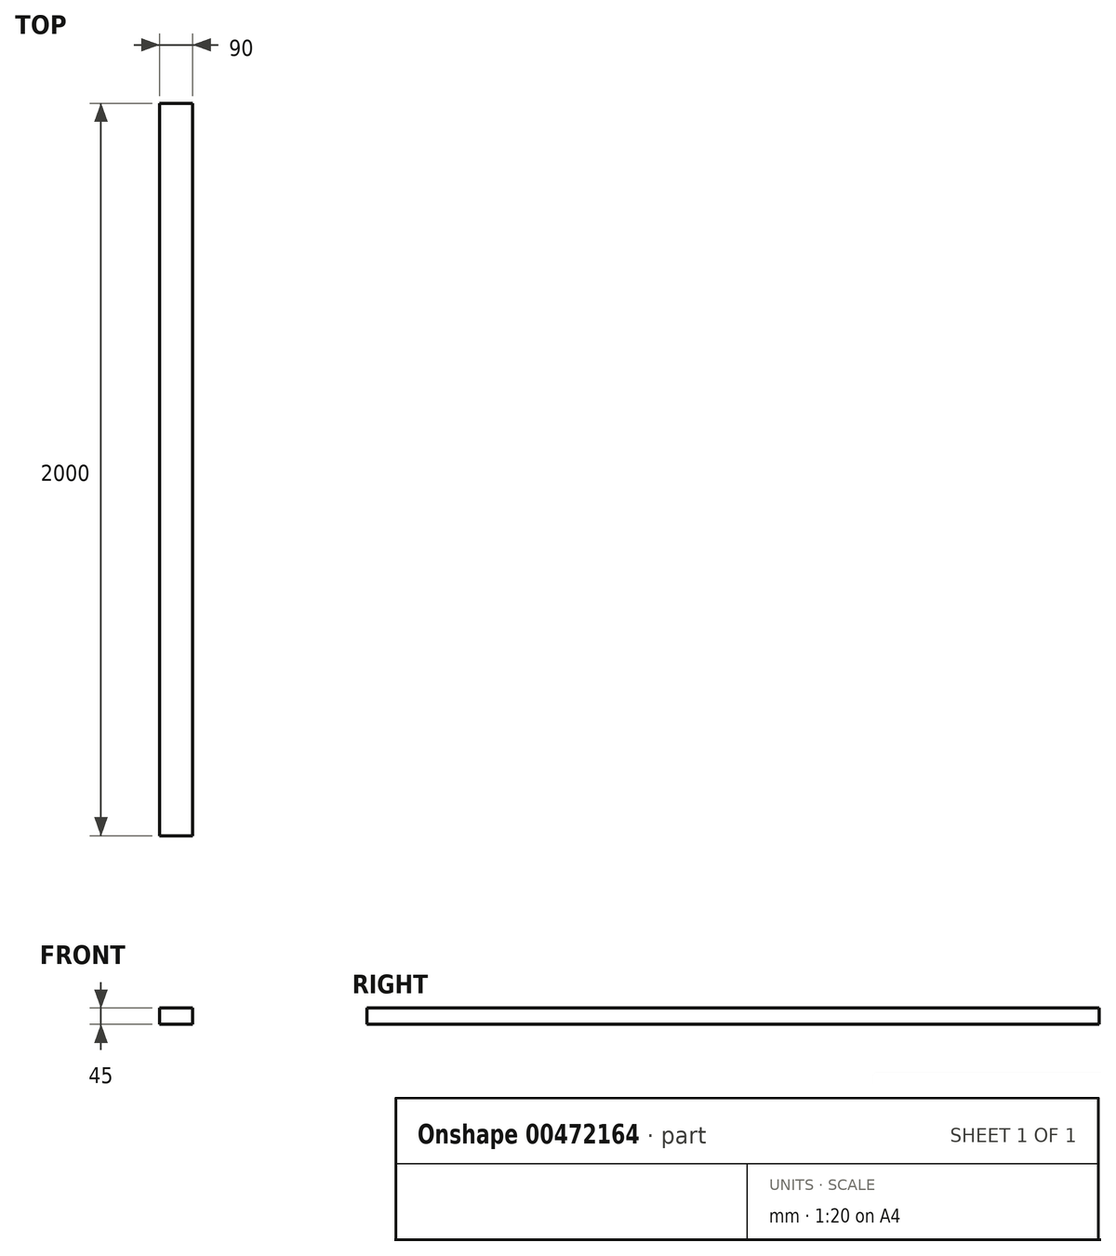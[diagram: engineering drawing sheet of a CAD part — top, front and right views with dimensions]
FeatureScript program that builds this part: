
annotation { "Feature Type Name" : "Feature", "Feature Type Description" : "" }
export const myFeature = defineFeature(function(context is Context, id is Id, definition is map)
    precondition{}
    {
        {
            var Q0;
            Q0=qCreatedBy(makeId("Front.planeOp"),FACE);
            var sketch = newSketch(context, id + "F0", { "sketchPlane" : qUnion([Q0])});
            skLineSegment(sketch, "E0.bottom", {"start": v(-45, 22.5) * mm, "end": v(45, 22.5) * mm});
            skLineSegment(sketch, "E0.top", {"start": v(-45, -22.5) * mm, "end": v(45, -22.5) * mm});
            skLineSegment(sketch, "E0.left", {"start": v(-45, 22.5) * mm, "end": v(-45, -22.5) * mm});
            skLineSegment(sketch, "E0.right", {"start": v(45, 22.5) * mm, "end": v(45, -22.5) * mm});
            skPoint(sketch, "E0.middle", {"position": v(0, 0) * mm});
            skSolve(sketch);
        }
        {
            var Q0;
            Q0=makeQuery(id+"F0.imprint","IMPRINT",FACE,{"disambiguationData":[TD([[makeQuery(id+"F0.imprint","IMPRINT",EDGE,{"derivedFrom":sQuery(id+"F0.wireOp",EDGE,"E0.bottom")}),-1.0]])]});
            extrude(context, id + "F1", {"entities" : qUnion([Q0]), "endBound" : BoundingType.SYMMETRIC, "depth" : 2000 * mm});
        }
    });
